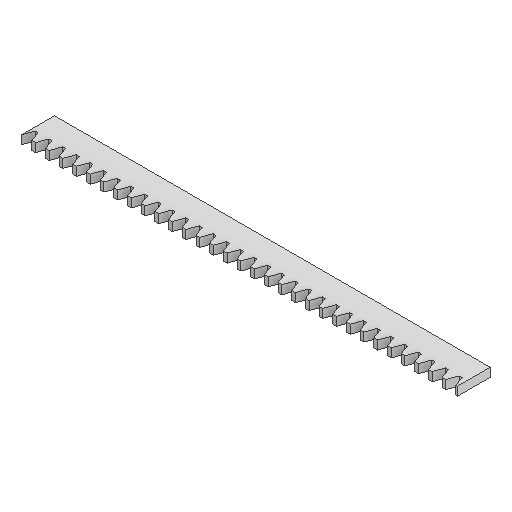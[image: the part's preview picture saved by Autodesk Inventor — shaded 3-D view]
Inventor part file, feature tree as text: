
AUTODESK INVENTOR PART (.ipt)
format: ipt  version: 2025.1 (Build 291241000, 241)  size: 248,320 bytes
history: native  units: mm
features: other x2, extrude x1, sketch x1
ambient origin geometry x8: Origin, YZ Plane, XZ Plane, XY Plane, X Axis, Y Axis, Z Axis, Center Point
bodies: Body1 (feature_tree)
feature tree (4):
  other  "Bryła1"
  extrude  "Wyciągnięcie proste1"  Depth=6.0mm TaperAngle=0.0deg
  sketch  "Szkic1"
  other  "Rack1.stp_1_"
